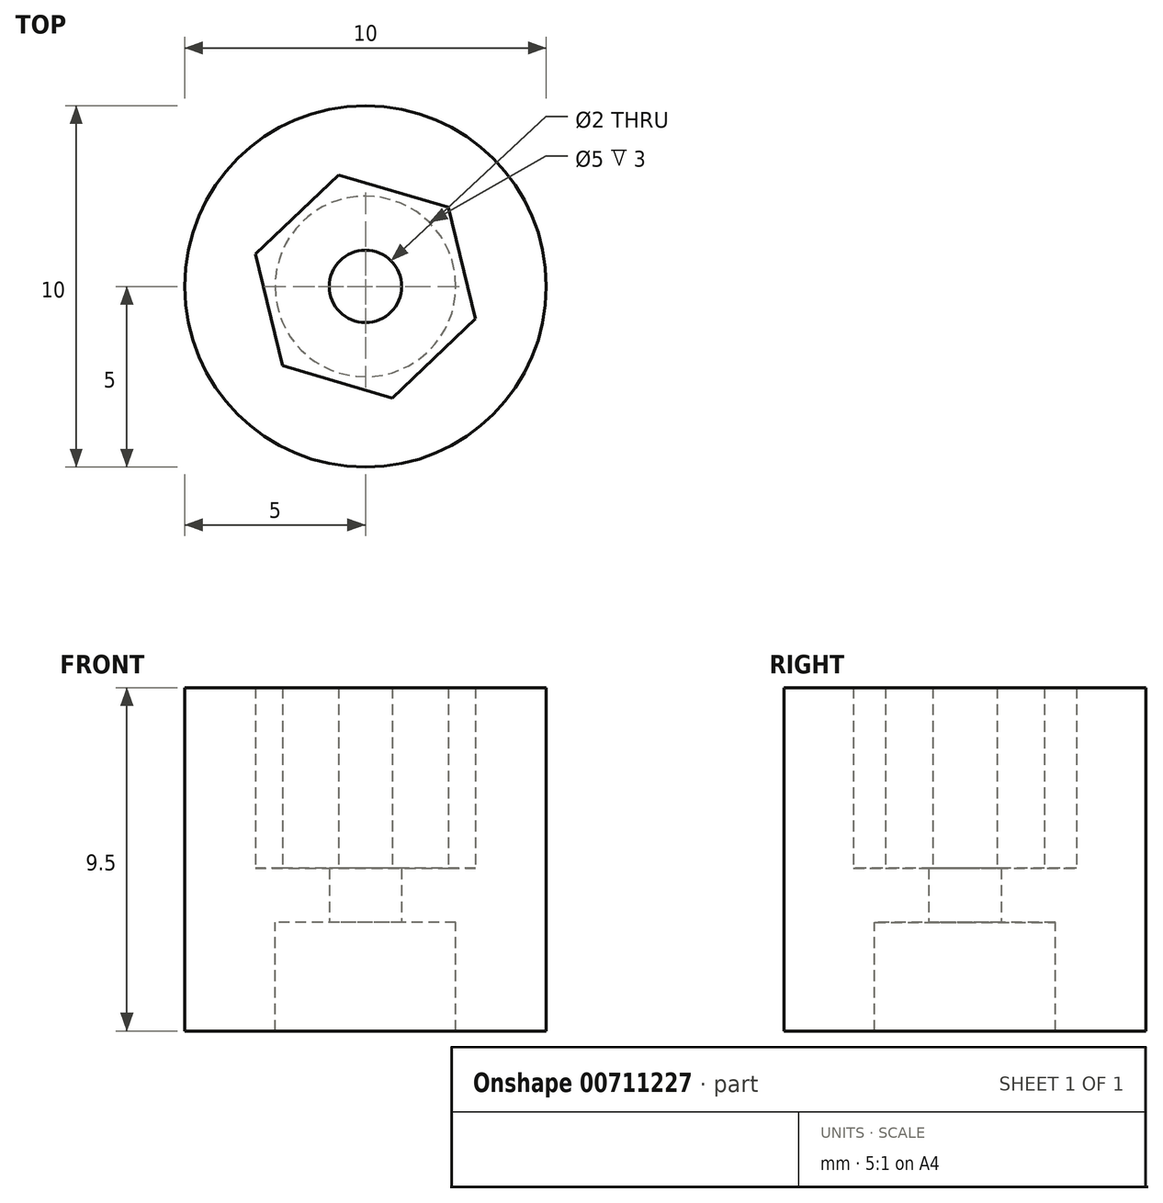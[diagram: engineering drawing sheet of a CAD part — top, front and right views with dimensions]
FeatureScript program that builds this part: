
annotation { "Feature Type Name" : "Feature", "Feature Type Description" : "" }
export const myFeature = defineFeature(function(context is Context, id is Id, definition is map)
    precondition{}
    {
        {
            var Q0;
            Q0=qCreatedBy(makeId("Top.planeOp"),FACE);
            var sketch = newSketch(context, id + "F0", { "sketchPlane" : qUnion([Q0])});
            skCircle(sketch, "E0", {"center": v(0, 0) * mm, "radius": 2.5 * mm});
            skCircle(sketch, "E1", {"center": v(0, 0) * mm, "radius": 5 * mm});
            skCircle(sketch, "E2", {"center": v(0, 0) * mm, "radius": 1 * mm});
            skSolve(sketch);
        }
        {
            var Q0;
            Q0=makeQuery(id+"F0.imprint","IMPRINT",FACE,{"disambiguationData":[TD([[makeQuery(id+"F0.imprint","IMPRINT",EDGE,{"derivedFrom":sQuery(id+"F0.wireOp",EDGE,"E0")}),-1.0]])]});
            var Q1;
            Q1=makeQuery(id+"F0.imprint","IMPRINT",FACE,{"disambiguationData":[TD([[makeQuery(id+"F0.imprint","IMPRINT",EDGE,{"derivedFrom":sQuery(id+"F0.wireOp",EDGE,"E0")}),1.0]])]});
            extrude(context, id + "F1", {"entities" : qUnion([Q0, Q1]), "depth" : 1.5 * mm, "offsetDistance" : 25 * mm});
        }
        {
            var Q0;
            Q0=makeQuery(id+"F0.imprint","IMPRINT",FACE,{"disambiguationData":[TD([[makeQuery(id+"F0.imprint","IMPRINT",EDGE,{"derivedFrom":sQuery(id+"F0.wireOp",EDGE,"E0")}),-1.0]])]});
            extrude(context, id + "F2", {"entities" : qUnion([Q0]), "operationType" : NewBodyOperationType.ADD, "oppositeDirection" : true, "depth" : 3 * mm, "offsetDistance" : 25 * mm});
        }
        {
            var Q0;
            Q0=makeQuery(id+"F1.opExtrude","CAP_FACE",FACE,{"disambiguationData":[OSD([sQuery(id+"F0.wireOp",EDGE,"E1"),sQuery(id+"F0.wireOp",EDGE,"E2")])],"isStart":false});
            var sketch = newSketch(context, id + "F3", { "sketchPlane" : qUnion([Q0])});
            skCircle(sketch, "E3.cCircle", {"center": v(0, 0) * mm, "radius": 2.75 * mm, "construction": true});
            skLineSegment(sketch, "E3.0", {"start": v(-0.75, 3.09) * mm, "end": v(2.3, 2.2) * mm});
            skLineSegment(sketch, "E3.1", {"start": v(2.3, 2.2) * mm, "end": v(3.05, -0.9) * mm});
            skLineSegment(sketch, "E3.2", {"start": v(3.05, -0.9) * mm, "end": v(0.75, -3.09) * mm});
            skLineSegment(sketch, "E3.3", {"start": v(0.75, -3.09) * mm, "end": v(-2.3, -2.2) * mm});
            skLineSegment(sketch, "E3.4", {"start": v(-2.3, -2.2) * mm, "end": v(-3.05, 0.9) * mm});
            skLineSegment(sketch, "E3.5", {"start": v(-3.05, 0.9) * mm, "end": v(-0.75, 3.09) * mm});
            skPoint(sketch, "E3.0.midPoint", {"position": v(0.77, 2.64) * mm});
            skSolve(sketch);
        }
        {
            var Q0;
            Q0=makeQuery(id+"F3.imprint","IMPRINT",FACE,{"disambiguationData":[TD([[makeQuery(id+"F3.imprint","IMPRINT",EDGE,{"derivedFrom":sQuery(id+"F3.wireOp",EDGE,"E3.0")}),1.0]])]});
            extrude(context, id + "F4", {"entities" : qUnion([Q0]), "operationType" : NewBodyOperationType.ADD, "depth" : 5 * mm, "offsetDistance" : 25 * mm});
        }
    });
